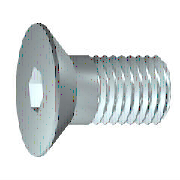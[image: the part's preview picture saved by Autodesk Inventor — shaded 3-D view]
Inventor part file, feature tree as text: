
AUTODESK INVENTOR PART (.ipt)
format: ipt  version: 2024 (Build 280153000, 153)  size: 185,344 bytes
history: native  units: mm (DEFAULTED — no unit token found)
features: other x1, extrude x1, plane x1
ambient origin geometry x7: Origin, YZ Plane, XY Plane, X Axis, Y Axis, Z Axis, Center Point
bodies: Solid1 (feature_tree)
feature tree (3):
  other  "Corps"
  extrude  "Rainure"  Depth=16.0mm
  plane  "Work Plane1"
